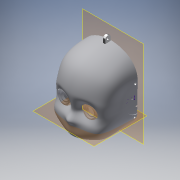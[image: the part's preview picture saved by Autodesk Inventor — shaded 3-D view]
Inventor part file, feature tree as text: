
AUTODESK INVENTOR PART (.ipt)
format: ipt  version: 2019 (Build 230136000, 136)  size: 7,706,624 bytes
history: native  units: in
note: dims shown in document units (in); Inventor stores cm internally (conversion verified against a paired STEP export)
features: sketch x32, extrude x24, other x18, plane x15, projected_geometry x7, mirror x6, surface_op x6, fillet x2, hole x2, thicken_offset x2, imported_body x2
ambient origin geometry x8: Origin, YZ Plane, XZ Plane, XY Plane, X Axis, Y Axis, Z Axis, Center Point
bodies: Solid6 (feature_tree), Solid2 (feature_tree)
feature tree (116):
  other  "rc_ist_009_p_077_09"
  other  "rc_ist_009_p_077_091"
  other  "Work Point1"
  other  "Work Point2"
  other  "Work Point3"
  other  "Work Point4"
  other  "Work Point5"
  other  "A_5"
  other  "A_6"
  other  "A_7"
  other  "A_8"
  other  "SIDE"
  other  "TOP"
  plane  "Work Plane4"
  plane  "Work Plane11"
  plane  "Work Plane7"
  plane  "Work Plane9"
  extrude  "Extrusion10"  Depth=0.9252in
  sketch  "Sketch11"  dims[d40=0.315in d41=0.315in]
  extrude  "Extrusion11"  Depth=0.315in
  plane  "Work Plane10"
  extrude  "Extrusion12"  Depth=1.063in TaperAngle=0.0deg
  mirror  "Mirror3"
  extrude  "Extrusion13"  Depth=1.8504in
  fillet  "Fillet1"  Radius=2.3622in
  fillet  "Fillet2"  Radius=0.3543in
  sketch  "Sketch15"  dims[d54=0.2756in d55=0.1969in d56=0.0in]
  extrude  "Extrusion14"  Depth=0.1969in TaperAngle=0.0deg
  extrude  "Extrusion15"  Depth=0.1969in TaperAngle=0.0deg
  extrude  "Extrusion16"  Depth=0.3937in
  extrude  "Extrusion17"  Depth=0.3937in
  extrude  "Extrusion18"  Depth=1.1811in
  extrude  "Extrusion19"  Depth=0.3937in
  hole  "Hole1"  [1 undecoded]
  hole  "Hole2"  [1 undecoded]
  extrude  "Extrusion22"  Depth=2.5591in
  extrude  "Extrusion23"  TaperAngle=150.0deg  [1 undecoded]
  extrude  "Extrusion24"  TaperAngle=60.0deg  [1 undecoded]
  extrude  "Extrusion25"  Depth=0.315in
  extrude  "Extrusion26"  Depth=0.3937in TaperAngle=0.0deg
  sketch  "Sketch34"  dims[d96=0.1969in d97=150.0deg]
  sketch  "3D Sketch2"
  surface_op  "Extend2"
  thicken_offset  "Thicken5"
  plane  "Work Plane12"
  extrude  "Extrusion27"  TaperAngle=150.0deg  [1 undecoded]
  plane  "Work Plane13"
  surface_op  "Extend3"
  thicken_offset  "Thicken6"
  mirror  "Mirror4"
  plane  "Work Plane14"
  plane  "Work Plane15"
  extrude  "Extrusion29"  TaperAngle=120.0deg  [1 undecoded]
  mirror  "Mirror5"
  plane  "Work Plane16"
  extrude  "Extrusion30"  TaperAngle=150.0deg  [1 undecoded]
  mirror  "Mirror6"
  extrude  "Extrusion31"  TaperAngle=120.0deg  [1 undecoded]
  plane  "Work Plane17"
  extrude  "Extrusion32"  Depth=0.7874in
  mirror  "Mirror8"
  extrude  "Extrusion33"  Depth=0.4331in
  extrude  "Extrusion34"  Depth=0.3937in
  mirror  "Mirror9"
  plane  "Work Plane19"
  sketch  "Sketch49"  dims[d134=0.1575in d135=0.0in]
  plane  "Work Plane20"
  extrude  "Extrusion35"  Depth=0.3937in
  plane  "Work Plane21"
  extrude  "Extrusion36"  Depth=0.7087in
  sketch  "3D Sketch1"
  other  "FRONT"
  imported_body  "Base1"
  imported_body  "Base2"
  plane  "Work Plane8"
  sketch  "Sketch10"  dims[d3=3.563in d35=0.9252in]
  sketch  "Sketch12"  dims[d42=0.315in d43=1.063in d44=0.0in]
  sketch  "Sketch13"  dims[d45=0.9252in d46=1.8504in d47=2.3622in d48=0.0in d49=0.3543in]
  sketch  "Sketch14"  dims[d50=0.3543in d52=0.1969in d53=0.0in]
  projected_geometry  "Projected Loop6"
  sketch  "Sketch16"  dims[d57=0.3937in d58=0.3937in]
  sketch  "Sketch17"  dims[d59=0.2362in d60=0.0in d61=0.3937in]
  projected_geometry  "Projected Loop7"
  projected_geometry  "Projected Loop8"
  projected_geometry  "Projected Loop9"
  sketch  "Sketch18"  dims[d62=180.0deg d63=1.1811in]
  projected_geometry  "Projected Loop10"
  sketch  "Sketch19"  dims[d64=90.0deg d65=0.3937in]
  projected_geometry  "Projected Loop11"
  sketch  "Sketch21"  dims[d66=90.0deg d67=3.937in d68=0.0in]
  sketch  "Sketch22"  dims[d73=0.3937in d75=3.937in d76=0.0in]
  sketch  "Sketch26"  dims[d77=3.937in d78=0.0in d82=2.5591in]
  sketch  "Sketch27"  dims[d83=2.5591in d84=150.0deg]
  sketch  "Sketch29"  dims[d85=0.315in d86=60.0deg]
  sketch  "Sketch30"  dims[d87=30.0deg d88=0.315in]
  sketch  "Sketch31"  dims[d89=60.0deg d90=0.3937in d91=0.0in]
  sketch  "Sketch32"  dims[d92=0.1969in d93=150.0deg]
  sketch  "Sketch33"  dims[d94=0.1969in d95=120.0deg]
  other  "Srf6"
  sketch  "Sketch35"  dims[d98=0.1969in d99=120.0deg]
  other  "Srf7"
  other  "Srf11"
  other  "Srf10"
  sketch  "Sketch38"  dims[d100=0.3937in d101=0.0in d108=0.7874in]
  sketch  "Sketch39"  dims[d109=0.2953in]
  sketch  "Sketch41"  dims[d110=0.2953in d111=0.2362in d112=0.1575in d113=0.0787in d114=90.0deg d115=0.315in d116=0.8108in d117=0.4331in]
  sketch  "Sketch42"  dims[d118=0.4724in d119=0.2362in d120=0.1575in d121=0.0787in d122=90.0deg d123=0.1969in d124=0.0in d127=0.3937in]
  sketch  "Sketch43"  dims[d128=0.1969in d129=0.0in d130=0.3937in]
  sketch  "Sketch44"  dims[d131=0.1969in d132=0.0in d133=0.7087in]
  projected_geometry  "Projected Loop12"
  sketch  "Sketch50"  dims[d136=0.5906in]
  sketch  "Sketch51"  dims[d137=0.1575in d138=0.0in d139=0.3937in d140=0.0in d153=0.1969in d154=0.0in d158=0.1181in d160=0.3937in d161=-0.815in d162=0.0in d163=0.0in d165=0.8465in d166=1.0625in d169=0.1969in d170=0.0in d171=0.1575in d172=0.1575in d173=0.1575in d185=0.3937in d190=0.0in d191=-1.6063in d192=0.315in d193=0.3937in d194=0.0787in d195=0.3937in d196=0.0in d197=1.7913in d200=0.315in d201=0.3937in d202=0.0in d203=0.0787in d204=0.3937in d205=0.0in d213=0.1378in d214=0.1969in d215=0.1181in d216=0.3937in d217=0.0in d218=0.2362in d219=0.1181in d220=0.0in d221=0.1378in d222=0.1969in d223=0.1378in d224=0.0787in d225=0.0in d226=0.2362in d227=0.1181in d228=0.0in d231=-0.375in d232=0.0394in d233=0.0197in d234=0.7874in d235=0.0in d236=2.3622in d237=0.0in]
  surface_op  "Boundary Patch2"
  surface_op  "Boundary Patch3"
  surface_op  "Boundary Patch6"
  surface_op  "Boundary Patch7"
note: 8 required parameter values undecoded (feature->parameter linkage not recoverable at this tier; creation-order binding heuristic only, values carry confidence <= 0.55)
